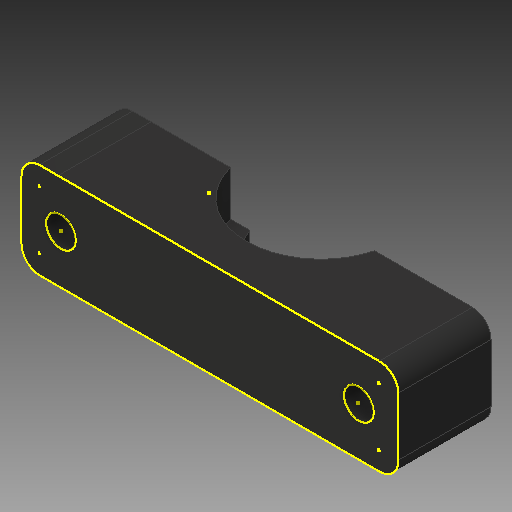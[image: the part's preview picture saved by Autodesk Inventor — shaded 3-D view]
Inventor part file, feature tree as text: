
AUTODESK INVENTOR PART (.ipt)
format: ipt  version: 2018 (Build 220112000, 112)  size: 142,848 bytes
history: native  units: mm
features: sketch x5, other x3
ambient origin geometry x8: Origin, YZ Plane, XZ Plane, XY Plane, X Axis, Y Axis, Z Axis, Center Point
bodies: Solid1 (feature_tree)
feature tree (8):
  other  "Hotend Clamp P1.ipt"
  other  "Solid1::Hotend Clamp P1.ipt"
  other  "TaggingFeature1"
  sketch  "Sketch1"  dims[d0=10.0mm]
  sketch  "Sketch2"
  sketch  "Sketch3"
  sketch  "Sketch4"
  sketch  "Sketch5"
